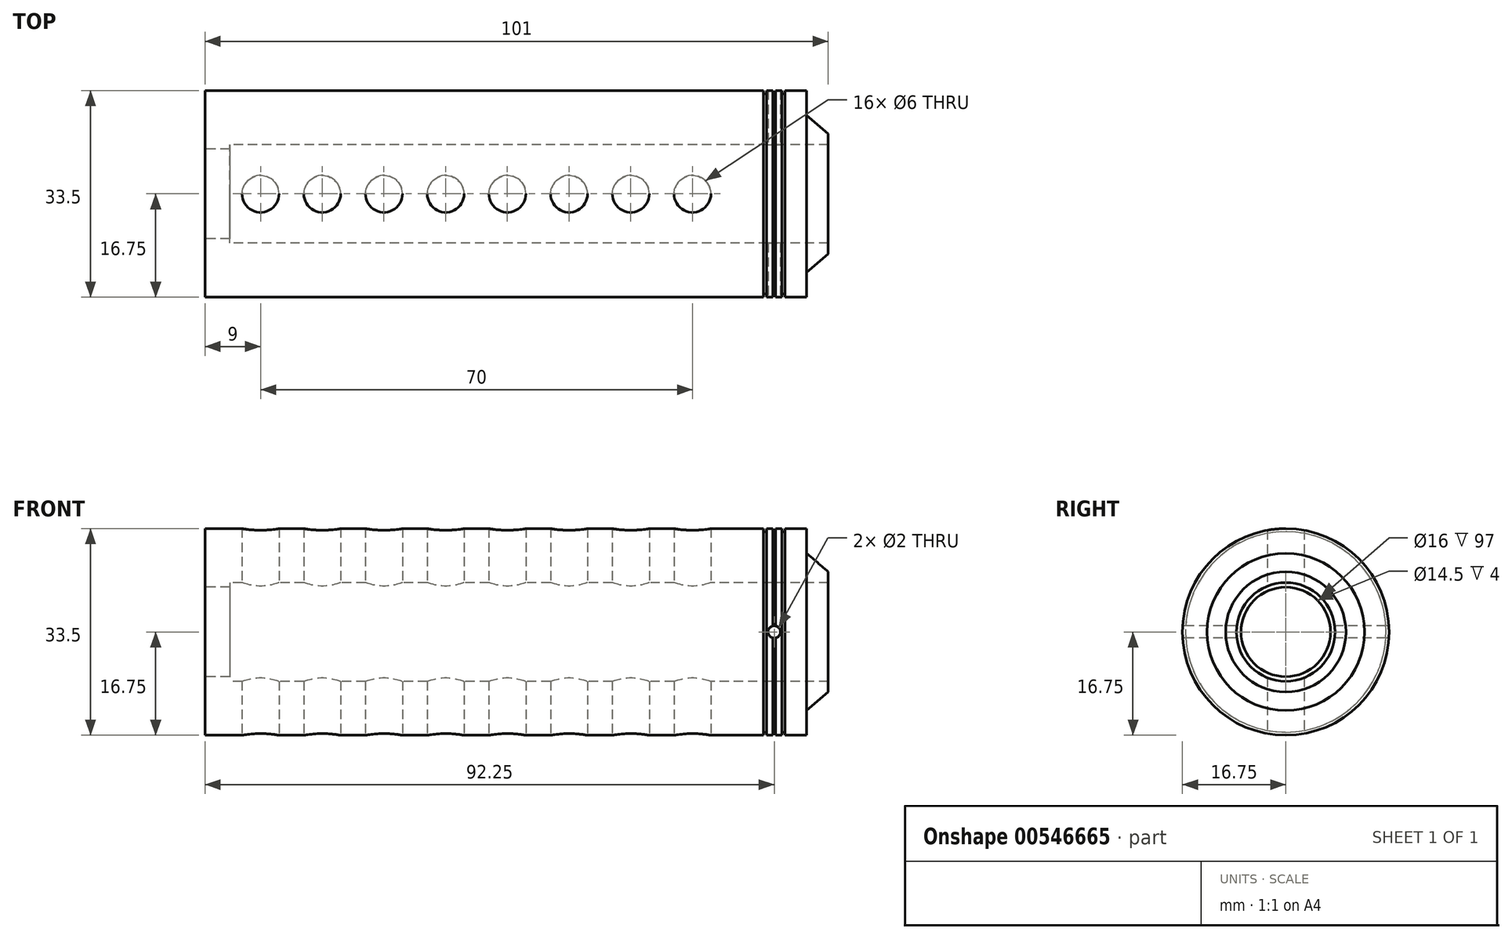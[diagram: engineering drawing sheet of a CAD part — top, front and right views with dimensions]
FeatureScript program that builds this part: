
annotation { "Feature Type Name" : "Feature", "Feature Type Description" : "" }
export const myFeature = defineFeature(function(context is Context, id is Id, definition is map)
    precondition{}
    {
        {
            var Q0;
            Q0=qCreatedBy(makeId("Front.planeOp"),FACE);
            var sketch = newSketch(context, id + "F0", { "sketchPlane" : qUnion([Q0])});
            skLineSegment(sketch, "E0", {"start": v(0, 0) * mm, "end": v(0, -16.75) * mm});
            skLineSegment(sketch, "E1", {"start": v(0, -16.75) * mm, "end": v(90.5, -16.75) * mm});
            skLineSegment(sketch, "E2", {"start": v(97.5, -16.75) * mm, "end": v(97.5, -12.75) * mm});
            skLineSegment(sketch, "E3", {"start": v(101, -8) * mm, "end": v(101, -9.75) * mm});
            skLineSegment(sketch, "E4", {"start": v(101, -9.75) * mm, "end": v(97.5, -12.75) * mm});
            skLineSegment(sketch, "E5", {"start": v(94, 3.53) * mm, "end": v(94, 0) * mm, "construction": true});
            skLineSegment(sketch, "E6", {"start": v(93.5, 3.88) * mm, "end": v(93.5, 0) * mm, "construction": true});
            skLineSegment(sketch, "E7.0", {"start": v(90.5, -16.25) * mm, "end": v(91, -16.25) * mm});
            skLineSegment(sketch, "E8.0", {"start": v(92.5, 3.88) * mm, "end": v(92.5, 0) * mm});
            skLineSegment(sketch, "E9.0", {"start": v(92, 3.88) * mm, "end": v(92, 0) * mm});
            skLineSegment(sketch, "E10.0", {"start": v(91, 3.88) * mm, "end": v(91, 0) * mm});
            skLineSegment(sketch, "E11.0", {"start": v(90.5, 3.88) * mm, "end": v(90.5, 0) * mm});
            skLineSegment(sketch, "E12", {"start": v(94, -16.75) * mm, "end": v(94, -16.25) * mm});
            skLineSegment(sketch, "E13", {"start": v(93.5, -16.75) * mm, "end": v(93.5, -16.25) * mm});
            skLineSegment(sketch, "E14.trimOffspring", {"start": v(92.5, -16.75) * mm, "end": v(93.5, -16.75) * mm});
            skLineSegment(sketch, "E15.trimOffspring", {"start": v(90.5, -16.25) * mm, "end": v(90.5, -16.75) * mm});
            skLineSegment(sketch, "E16.trimOffspring", {"start": v(91, -16.25) * mm, "end": v(91, -16.75) * mm});
            skLineSegment(sketch, "E17.trimOffspring", {"start": v(92, -16.25) * mm, "end": v(92, -16.75) * mm});
            skLineSegment(sketch, "E18.trimOffspring", {"start": v(92.5, -16.25) * mm, "end": v(92.5, -16.75) * mm});
            skLineSegment(sketch, "E19.trimOffspring", {"start": v(93.5, -16.25) * mm, "end": v(93.5, -21.89) * mm, "construction": true});
            skLineSegment(sketch, "E20.trimOffspring", {"start": v(94, -16.25) * mm, "end": v(94, -21.24) * mm, "construction": true});
            skLineSegment(sketch, "E21.trimOffspring", {"start": v(94, -16.75) * mm, "end": v(97.5, -16.75) * mm});
            skLineSegment(sketch, "E22.trimOffspring", {"start": v(93.5, -16.25) * mm, "end": v(94, -16.25) * mm});
            skLineSegment(sketch, "E23.trimOffspring", {"start": v(92, -16.25) * mm, "end": v(92.5, -16.25) * mm});
            skLineSegment(sketch, "E24.trimOffspring", {"start": v(91, -16.75) * mm, "end": v(92, -16.75) * mm});
            skLineSegment(sketch, "E25.0", {"start": v(101, -8) * mm, "end": v(4, -8) * mm});
            skLineSegment(sketch, "E26", {"start": v(0, 0) * mm, "end": v(4, 0) * mm});
            skLineSegment(sketch, "E27", {"start": v(4, 0) * mm, "end": v(4, -8) * mm});
            skSolve(sketch);
        }
        {
            var Q0;
            Q0=qSketchRegion(id+"F0",true);
            var Q1;
            Q1=sQuery(id+"F0.wireOp",EDGE,"E26");
            revolve(context, id + "F1", {"entities" : qUnion([Q0]), "axis" : qUnion([Q1]), "revolveType" : RevolveType.FULL});
        }
        {
            var Q0;
            Q0=qCreatedBy(makeId("Front.planeOp"),FACE);
            var sketch = newSketch(context, id + "F2", { "sketchPlane" : qUnion([Q0])});
            skLineSegment(sketch, "E28", {"start": v(69.11, 0) * mm, "end": v(107.74, 0) * mm, "construction": true});
            skCircle(sketch, "E29", {"center": v(92.25, 0) * mm, "radius": 1 * mm});
            skSolve(sketch);
        }
        {
            var Q0;
            Q0=qSketchRegion(id+"F2",true);
            extrude(context, id + "F3", {"entities" : qUnion([Q0]), "operationType" : NewBodyOperationType.REMOVE, "endBound" : BoundingType.SYMMETRIC, "oppositeDirection" : true, "depth" : 50 * mm});
        }
        {
            var Q0;
            Q0=makeQuery(id+"F1.opRevolve","SWEPT_FACE",FACE,{"disambiguationData":[OSD([sQuery(id+"F0.wireOp",EDGE,"E0")])]});
            var sketch = newSketch(context, id + "F4", { "sketchPlane" : qUnion([Q0])});
            skCircle(sketch, "E30", {"center": v(0, 0) * mm, "radius": 7.25 * mm});
            skSolve(sketch);
        }
        {
            var Q0;
            Q0=qSketchRegion(id+"F4",true);
            extrude(context, id + "F5", {"entities" : qUnion([Q0]), "operationType" : NewBodyOperationType.REMOVE, "oppositeDirection" : true, "depth" : 2.5 * mm});
        }
        {
            var Q0;
            Q0=qCreatedBy(makeId("Top.planeOp"),FACE);
            var sketch = newSketch(context, id + "F6", { "sketchPlane" : qUnion([Q0])});
            skLineSegment(sketch, "E31", {"start": v(9, 18.99) * mm, "end": v(9, -20.5) * mm, "construction": true});
            skLineSegment(sketch, "E32.0", {"start": v(19, 18.99) * mm, "end": v(19, -20.5) * mm});
            skLineSegment(sketch, "E33.0", {"start": v(29, 18.99) * mm, "end": v(29, -20.5) * mm});
            skLineSegment(sketch, "E34.0", {"start": v(39, 18.99) * mm, "end": v(39, -20.5) * mm});
            skLineSegment(sketch, "E35.0", {"start": v(49, 18.99) * mm, "end": v(49, -20.5) * mm});
            skLineSegment(sketch, "E36.0", {"start": v(59, 18.99) * mm, "end": v(59, -20.5) * mm});
            skLineSegment(sketch, "E37.0", {"start": v(69, 18.99) * mm, "end": v(69, -20.5) * mm});
            skLineSegment(sketch, "E38.0", {"start": v(79, 18.99) * mm, "end": v(79, -20.5) * mm});
            skCircle(sketch, "E39", {"center": v(9, 0) * mm, "radius": 3 * mm});
            skCircle(sketch, "E40", {"center": v(19, 0) * mm, "radius": 3 * mm});
            skCircle(sketch, "E41", {"center": v(29, 0) * mm, "radius": 3 * mm});
            skCircle(sketch, "E42", {"center": v(39, 0) * mm, "radius": 3 * mm});
            skCircle(sketch, "E43", {"center": v(49, 0) * mm, "radius": 3 * mm});
            skCircle(sketch, "E44", {"center": v(59, 0) * mm, "radius": 3 * mm});
            skCircle(sketch, "E45", {"center": v(69, 0) * mm, "radius": 3 * mm});
            skCircle(sketch, "E46", {"center": v(79, 0) * mm, "radius": 3 * mm});
            skSolve(sketch);
        }
        {
            var Q0;
            Q0=qSketchRegion(id+"F6",true);
            extrude(context, id + "F7", {"entities" : qUnion([Q0]), "operationType" : NewBodyOperationType.REMOVE, "endBound" : BoundingType.SYMMETRIC, "depth" : 50 * mm});
        }
        {
            var Q0;
            Q0=makeQuery(id+"F5.boolean.opBoolean","COPY",FACE,{"derivedFrom":makeQuery(id+"F5.opExtrude","CAP_FACE",FACE,{"disambiguationData":[OSD([sQuery(id+"F4.wireOp",EDGE,"E30")])],"isStart":false})});
            var sketch = newSketch(context, id + "F8", { "sketchPlane" : qUnion([Q0])});
            skCircle(sketch, "E47.0", {"center": v(0, 0) * mm, "radius": 7.25 * mm});
            skSolve(sketch);
        }
        {
            var Q0;
            Q0=qSketchRegion(id+"F8",true);
            extrude(context, id + "F9", {"entities" : qUnion([Q0]), "operationType" : NewBodyOperationType.REMOVE, "oppositeDirection" : true, "depth" : 25 * mm});
        }
    });
